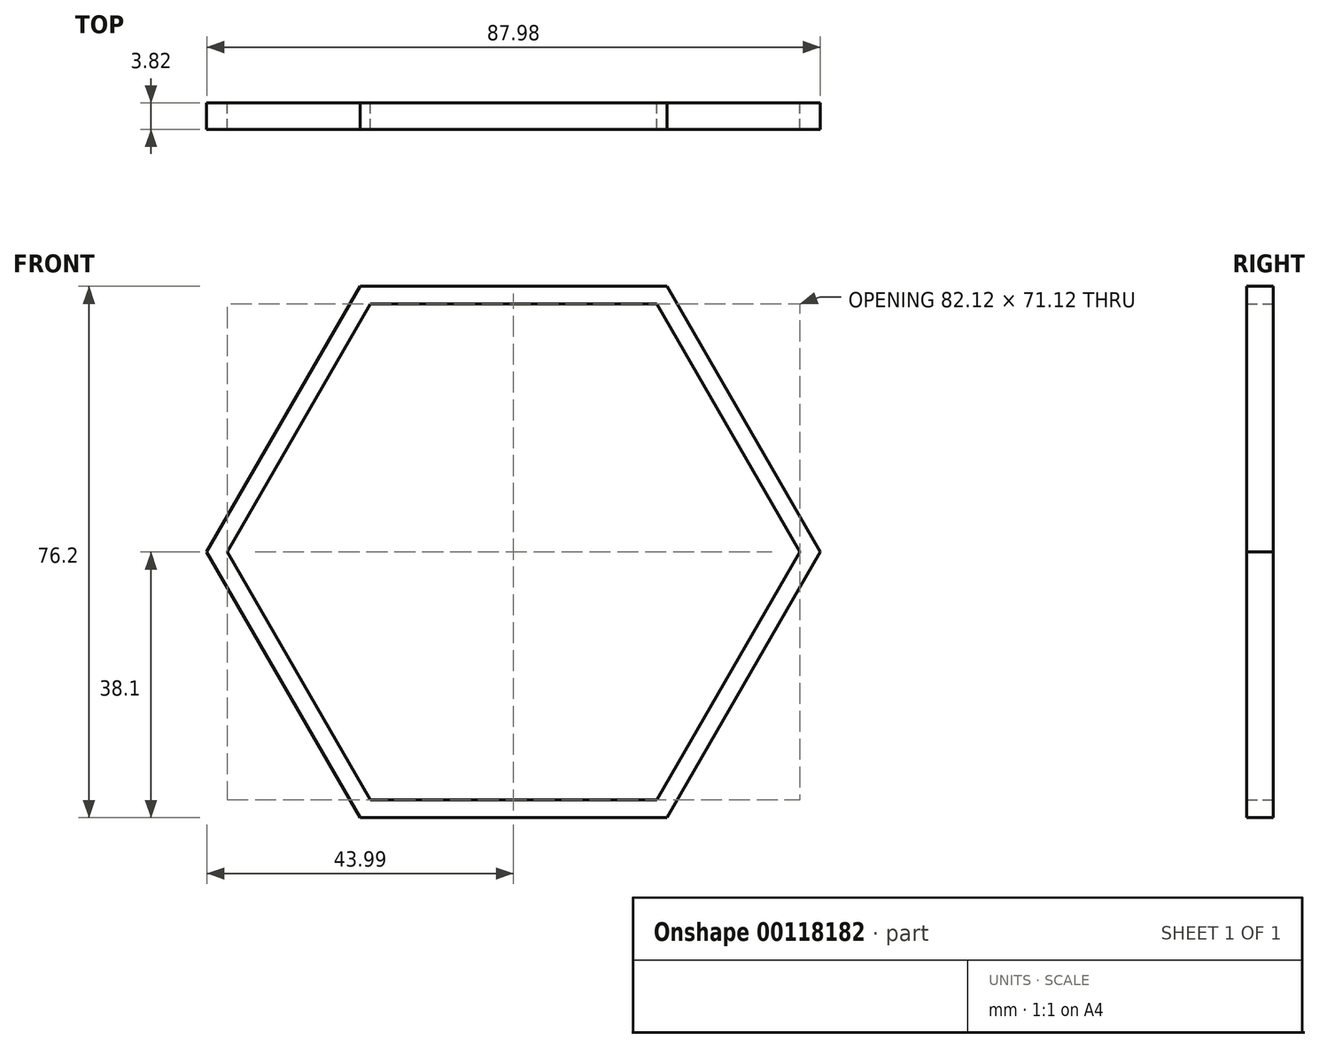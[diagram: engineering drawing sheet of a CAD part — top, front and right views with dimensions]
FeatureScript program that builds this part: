
annotation { "Feature Type Name" : "Feature", "Feature Type Description" : "" }
export const myFeature = defineFeature(function(context is Context, id is Id, definition is map)
    precondition{}
    {
        {
            var Q0;
            Q0=qCreatedBy(makeId("Front.planeOp"),FACE);
            var sketch = newSketch(context, id + "F0", { "sketchPlane" : qUnion([Q0])});
            skCircle(sketch, "E0.cCircle", {"center": v(0, 0) * mm, "radius": 35.56 * mm, "construction": true});
            skLineSegment(sketch, "E0.0", {"start": v(-20.53, 35.56) * mm, "end": v(20.53, 35.56) * mm});
            skLineSegment(sketch, "E0.1", {"start": v(20.53, 35.56) * mm, "end": v(41.06, 0) * mm});
            skLineSegment(sketch, "E0.2", {"start": v(41.06, 0) * mm, "end": v(20.53, -35.56) * mm});
            skLineSegment(sketch, "E0.3", {"start": v(20.53, -35.56) * mm, "end": v(-20.53, -35.56) * mm});
            skLineSegment(sketch, "E0.4", {"start": v(-20.53, -35.56) * mm, "end": v(-41.06, 0) * mm});
            skLineSegment(sketch, "E0.5", {"start": v(-41.06, 0) * mm, "end": v(-20.53, 35.56) * mm});
            skPoint(sketch, "E0.0.midPoint", {"position": v(0, 35.56) * mm});
            skLineSegment(sketch, "E1.0", {"start": v(22, -38.1) * mm, "end": v(-22, -38.1) * mm});
            skLineSegment(sketch, "E1.1", {"start": v(-44, 0) * mm, "end": v(-22, 38.1) * mm});
            skLineSegment(sketch, "E1.2", {"start": v(-22, 38.1) * mm, "end": v(22, 38.1) * mm});
            skLineSegment(sketch, "E1.3", {"start": v(-22, -38.1) * mm, "end": v(-44, 0) * mm});
            skLineSegment(sketch, "E1.4", {"start": v(22, 38.1) * mm, "end": v(44, 0) * mm});
            skLineSegment(sketch, "E1.5", {"start": v(44, 0) * mm, "end": v(22, -38.1) * mm});
            skSolve(sketch);
        }
        {
            var Q0;
            Q0=makeQuery(id+"F0.imprint","IMPRINT",FACE,{"disambiguationData":[TD([[makeQuery(id+"F0.imprint","IMPRINT",EDGE,{"derivedFrom":sQuery(id+"F0.wireOp",EDGE,"E0.0")}),1.0]])]});
            extrude(context, id + "F1", {"entities" : qUnion([Q0]), "endBound" : BoundingType.SYMMETRIC, "depth" : 3.8 * mm});
        }
    });
